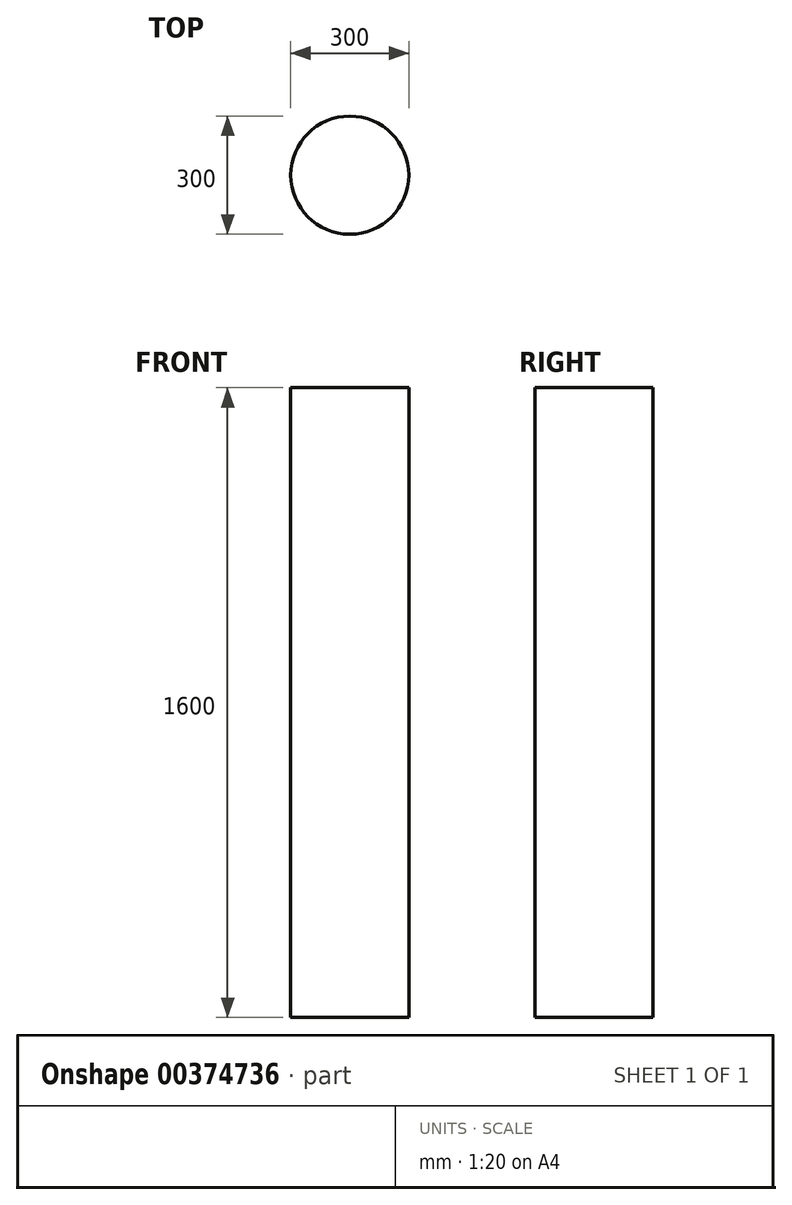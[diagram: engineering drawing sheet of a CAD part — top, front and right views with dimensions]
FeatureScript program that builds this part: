
annotation { "Feature Type Name" : "Feature", "Feature Type Description" : "" }
export const myFeature = defineFeature(function(context is Context, id is Id, definition is map)
    precondition{}
    {
        {
            var Q0;
            Q0=qCreatedBy(makeId("Top.planeOp"),FACE);
            var sketch = newSketch(context, id + "F0", { "sketchPlane" : qUnion([Q0])});
            skCircle(sketch, "E0", {"center": v(0, 0) * mm, "radius": 150 * mm});
            skSolve(sketch);
        }
        {
            var Q0;
            Q0=makeQuery(id+"F0.imprint","IMPRINT",FACE,{"disambiguationData":[TD([[makeQuery(id+"F0.imprint","IMPRINT",EDGE,{"derivedFrom":sQuery(id+"F0.wireOp",EDGE,"E0")}),1.0]])]});
            extrude(context, id + "F1", {"entities" : qUnion([Q0]), "depth" : 1600 * mm});
        }
    });
